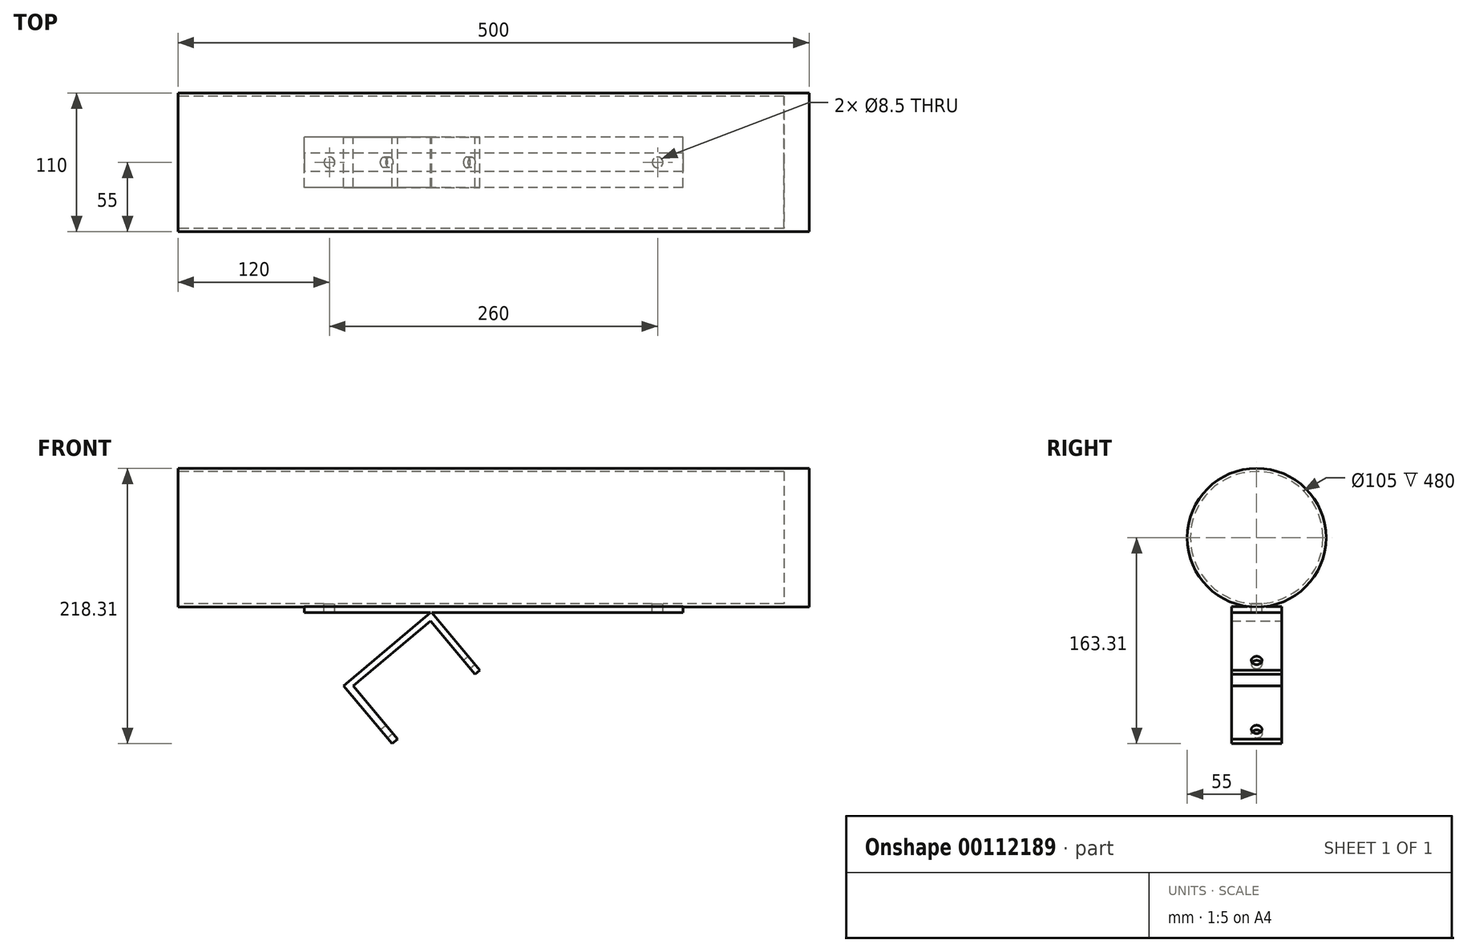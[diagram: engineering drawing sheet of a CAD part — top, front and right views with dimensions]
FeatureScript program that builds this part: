
annotation { "Feature Type Name" : "Feature", "Feature Type Description" : "" }
export const myFeature = defineFeature(function(context is Context, id is Id, definition is map)
    precondition{}
    {
        {
            var Q0;
            Q0=qCreatedBy(makeId("Front.planeOp"),FACE);
            var sketch = newSketch(context, id + "F0", { "sketchPlane" : qUnion([Q0])});
            skLineSegment(sketch, "E0.bottom", {"start": v(0, 0) * mm, "end": v(-199, 0) * mm});
            skLineSegment(sketch, "E0.top", {"start": v(0, 5) * mm, "end": v(-300, 5) * mm});
            skLineSegment(sketch, "E0.left", {"start": v(0, 0) * mm, "end": v(0, 5) * mm});
            skLineSegment(sketch, "E0.right", {"start": v(-300, 0) * mm, "end": v(-300, 5) * mm});
            skLineSegment(sketch, "E1", {"start": v(-200, 0) * mm, "end": v(-268.94, -57.85) * mm});
            skLineSegment(sketch, "E2", {"start": v(-268.94, -57.85) * mm, "end": v(-230.38, -103.81) * mm});
            skLineSegment(sketch, "E3", {"start": v(-230.38, -103.81) * mm, "end": v(-225.96, -100.1) * mm});
            skLineSegment(sketch, "E4", {"start": v(-225.96, -100.1) * mm, "end": v(-261.31, -57.97) * mm});
            skLineSegment(sketch, "E5", {"start": v(-261.31, -57.97) * mm, "end": v(-200.03, -6.55) * mm});
            skLineSegment(sketch, "E6", {"start": v(-200.03, -6.55) * mm, "end": v(-164.68, -48.68) * mm});
            skLineSegment(sketch, "E7", {"start": v(-164.68, -48.68) * mm, "end": v(-160.85, -45.47) * mm});
            skLineSegment(sketch, "E8", {"start": v(-160.85, -45.47) * mm, "end": v(-199, 0) * mm});
            skLineSegment(sketch, "E9.trimOffspring", {"start": v(-200, 0) * mm, "end": v(-300, 0) * mm});
            skSolve(sketch);
        }
        {
            var Q0;
            Q0=makeQuery(id+"F0.imprint","IMPRINT",FACE,{"disambiguationData":[TD([[makeQuery(id+"F0.imprint","IMPRINT",EDGE,{"derivedFrom":sQuery(id+"F0.wireOp",EDGE,"E0.bottom")}),-1.0]])]});
            extrude(context, id + "F1", {"entities" : qUnion([Q0]), "depth" : 40 * mm});
        }
        {
            var Q0;
            Q0=makeQuery(id+"F1.opExtrude","SWEPT_FACE",FACE,{"disambiguationData":[OSD([sQuery(id+"F0.wireOp",EDGE,"E0.top")])]});
            var sketch = newSketch(context, id + "F2", { "sketchPlane" : qUnion([Q0])});
            skPoint(sketch, "E10", {"position": v(-280, -20) * mm});
            skPoint(sketch, "E10.positionSnap0", {"position": v(-300, -20) * mm});
            skPoint(sketch, "E11", {"position": v(-20, -20) * mm});
            skPoint(sketch, "E11.positionSnap0", {"position": v(0, -20) * mm});
            skSolve(sketch);
        }
        {
            var Q0;
            Q0=makeQuery(id+"F1.opExtrude","SWEPT_FACE",FACE,{"disambiguationData":[OSD([sQuery(id+"F0.wireOp",EDGE,"E2")])]});
            var sketch = newSketch(context, id + "F3", { "sketchPlane" : qUnion([Q0])});
            skPoint(sketch, "E12", {"position": v(20, 78.56) * mm});
            skPoint(sketch, "E12.positionSnap0", {"position": v(20, 68.56) * mm});
            skSolve(sketch);
        }
        {
            var Q0;
            Q0=sQuery(id+"F3.wireOp",VERTEX,"E12");
            var Q1;
            Q1=makeQuery(id+"F1.opExtrude","SWEPT_BODY",BODY,{"disambiguationData":[OSD([sQuery(id+"F0.wireOp",EDGE,"E0.bottom"),sQuery(id+"F0.wireOp",EDGE,"E0.top"),sQuery(id+"F0.wireOp",EDGE,"E0.left"),sQuery(id+"F0.wireOp",EDGE,"E0.right"),sQuery(id+"F0.wireOp",EDGE,"E1"),sQuery(id+"F0.wireOp",EDGE,"E2"),sQuery(id+"F0.wireOp",EDGE,"E3"),sQuery(id+"F0.wireOp",EDGE,"E4"),sQuery(id+"F0.wireOp",EDGE,"E5"),sQuery(id+"F0.wireOp",EDGE,"E6"),sQuery(id+"F0.wireOp",EDGE,"E7"),sQuery(id+"F0.wireOp",EDGE,"E8"),sQuery(id+"F0.wireOp",EDGE,"E9.trimOffspring")])]});
            hole(context, id + "F4", {"style" : HoleStyle.SIMPLE, "endStyle" : HoleEndStyle.BLIND, "standardTappedOrClearance" : lookupTablePath({ "standard" : "ISO", "size" : "8.5", "type" : "Drilled" }), "standardBlindInLast" : lookupTablePath({ "standard" : "ISO", "size" : "8.5", "type" : "Drilled" }), "holeDiameter" : 8.5 * mm, "holeDepth" : 100 * mm, "locations" : qUnion([Q0]), "scope" : qUnion([Q1])});
        }
        {
            var Q0;
            Q0=qCreatedBy(makeId("Right.planeOp"),FACE);
            var sketch = newSketch(context, id + "F5", { "sketchPlane" : qUnion([Q0])});
            skCircle(sketch, "E13", {"center": v(-20, 59.5) * mm, "radius": 55 * mm});
            skSolve(sketch);
        }
        {
            var Q0;
            Q0=makeQuery(id+"F5.imprint","IMPRINT",FACE,{"disambiguationData":[TD([[makeQuery(id+"F5.imprint","IMPRINT",EDGE,{"derivedFrom":sQuery(id+"F5.wireOp",EDGE,"E13")}),1.0]])]});
            extrude(context, id + "F6", {"entities" : qUnion([Q0]), "operationType" : NewBodyOperationType.ADD, "depth" : 100 * mm, "hasSecondDirection" : true, "secondDirectionOppositeDirection" : true, "secondDirectionDepth" : 400 * mm});
        }
        {
            var Q0;
            Q0=makeQuery(id+"F6.opExtrude","CAP_FACE",FACE,{"disambiguationData":[OSD([sQuery(id+"F5.wireOp",EDGE,"E13")])],"isStart":true});
            var sketch = newSketch(context, id + "F7", { "sketchPlane" : qUnion([Q0])});
            skCircle(sketch, "E14", {"center": v(20, 59.5) * mm, "radius": 52.5 * mm});
            skSolve(sketch);
        }
        {
            var Q0;
            Q0=makeQuery(id+"F7.imprint","IMPRINT",FACE,{"disambiguationData":[TD([[makeQuery(id+"F7.imprint","IMPRINT",EDGE,{"derivedFrom":sQuery(id+"F7.wireOp",EDGE,"E14")}),1.0]])]});
            extrude(context, id + "F8", {"entities" : qUnion([Q0]), "operationType" : NewBodyOperationType.REMOVE, "oppositeDirection" : true, "depth" : 480 * mm});
        }
        {
            var Q0;
            Q0=sQuery(id+"F2.wireOp",VERTEX,"E10");
            var Q1;
            Q1=sQuery(id+"F2.wireOp",VERTEX,"E11");
            var Q2;
            Q2=makeQuery(id+"F1.opExtrude","SWEPT_BODY",BODY,{"disambiguationData":[OSD([sQuery(id+"F0.wireOp",EDGE,"E0.bottom"),sQuery(id+"F0.wireOp",EDGE,"E0.top"),sQuery(id+"F0.wireOp",EDGE,"E0.left"),sQuery(id+"F0.wireOp",EDGE,"E0.right"),sQuery(id+"F0.wireOp",EDGE,"E1"),sQuery(id+"F0.wireOp",EDGE,"E2"),sQuery(id+"F0.wireOp",EDGE,"E3"),sQuery(id+"F0.wireOp",EDGE,"E4"),sQuery(id+"F0.wireOp",EDGE,"E5"),sQuery(id+"F0.wireOp",EDGE,"E6"),sQuery(id+"F0.wireOp",EDGE,"E7"),sQuery(id+"F0.wireOp",EDGE,"E8"),sQuery(id+"F0.wireOp",EDGE,"E9.trimOffspring")])]});
            hole(context, id + "F9", {"style" : HoleStyle.SIMPLE, "endStyle" : HoleEndStyle.BLIND, "standardTappedOrClearance" : lookupTablePath({ "standard" : "ISO", "size" : "8.5", "type" : "Drilled" }), "standardBlindInLast" : lookupTablePath({ "standard" : "ISO", "size" : "8.5", "type" : "Drilled" }), "holeDiameter" : 8.5 * mm, "holeDepth" : 30 * mm, "locations" : qUnion([Q0, Q1]), "scope" : qUnion([Q2])});
        }
        {
            var Q0;
            Q0=sQuery(id+"F2.wireOp",VERTEX,"E10");
            var Q1;
            Q1=sQuery(id+"F2.wireOp",VERTEX,"E11");
            var Q2;
            Q2=makeQuery(id+"F1.opExtrude","SWEPT_BODY",BODY,{"disambiguationData":[OSD([sQuery(id+"F0.wireOp",EDGE,"E0.bottom"),sQuery(id+"F0.wireOp",EDGE,"E0.top"),sQuery(id+"F0.wireOp",EDGE,"E0.left"),sQuery(id+"F0.wireOp",EDGE,"E0.right"),sQuery(id+"F0.wireOp",EDGE,"E1"),sQuery(id+"F0.wireOp",EDGE,"E2"),sQuery(id+"F0.wireOp",EDGE,"E3"),sQuery(id+"F0.wireOp",EDGE,"E4"),sQuery(id+"F0.wireOp",EDGE,"E5"),sQuery(id+"F0.wireOp",EDGE,"E6"),sQuery(id+"F0.wireOp",EDGE,"E7"),sQuery(id+"F0.wireOp",EDGE,"E8"),sQuery(id+"F0.wireOp",EDGE,"E9.trimOffspring")])]});
            hole(context, id + "F10", {"style" : HoleStyle.SIMPLE, "endStyle" : HoleEndStyle.BLIND, "oppositeDirection" : true, "standardTappedOrClearance" : lookupTablePath({ "standard" : "ISO", "size" : "8.5", "type" : "Drilled" }), "standardBlindInLast" : lookupTablePath({ "standard" : "ISO", "size" : "8.5", "type" : "Drilled" }), "holeDiameter" : 8.5 * mm, "holeDepth" : 30 * mm, "locations" : qUnion([Q0, Q1]), "scope" : qUnion([Q2])});
        }
    });
